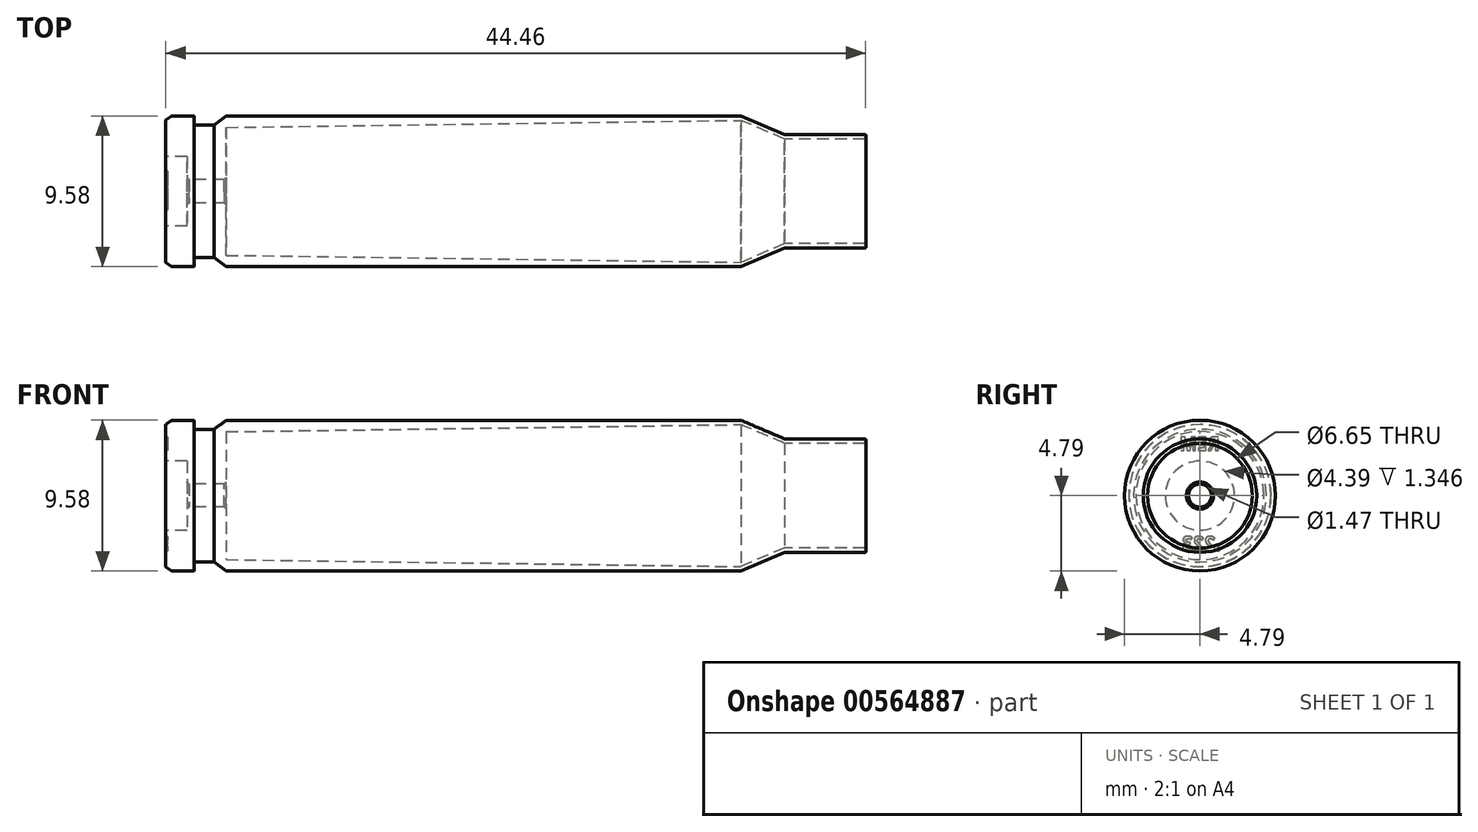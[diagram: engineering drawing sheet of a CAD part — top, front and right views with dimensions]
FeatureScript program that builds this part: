
annotation { "Feature Type Name" : "Feature", "Feature Type Description" : "" }
export const myFeature = defineFeature(function(context is Context, id is Id, definition is map)
    precondition{}
    {
        {
            var Q0;
            Q0=qCreatedBy(makeId("Front.planeOp"),FACE);
            var sketch = newSketch(context, id + "F0", { "sketchPlane" : qUnion([Q0])});
            skLineSegment(sketch, "E0", {"start": v(-35.9, 0) * mm, "end": v(-35.9, 4.52) * mm});
            skLineSegment(sketch, "E1", {"start": v(-35.9, 4.52) * mm, "end": v(-35.52, 4.79) * mm});
            skLineSegment(sketch, "E2", {"start": v(-35.52, 4.79) * mm, "end": v(-34.09, 4.79) * mm});
            skLineSegment(sketch, "E3", {"start": v(-34.09, 4.79) * mm, "end": v(-34.09, 4.22) * mm});
            skLineSegment(sketch, "E4", {"start": v(-34.09, 4.22) * mm, "end": v(-32.84, 4.22) * mm});
            skLineSegment(sketch, "E5", {"start": v(-32.84, 4.22) * mm, "end": v(-32.05, 4.79) * mm});
            skLineSegment(sketch, "E6", {"start": v(-32.05, 4.79) * mm, "end": v(0.63, 4.79) * mm});
            skLineSegment(sketch, "E7", {"start": v(0.63, 4.79) * mm, "end": v(3.4, 3.6) * mm});
            skLineSegment(sketch, "E8", {"start": v(3.4, 3.6) * mm, "end": v(8.56, 3.6) * mm});
            skLineSegment(sketch, "E9", {"start": v(8.56, 3.6) * mm, "end": v(8.56, 3.33) * mm});
            skLineSegment(sketch, "E10", {"start": v(8.56, 3.33) * mm, "end": v(3.4, 3.33) * mm});
            skLineSegment(sketch, "E11", {"start": v(3.4, 3.33) * mm, "end": v(0.63, 4.5) * mm});
            skLineSegment(sketch, "E12", {"start": v(0.63, 4.5) * mm, "end": v(-32.05, 4.06) * mm});
            skLineSegment(sketch, "E13", {"start": v(-32.05, 4.06) * mm, "end": v(-32.05, 0) * mm});
            skLineSegment(sketch, "E14", {"start": v(-32.05, 0) * mm, "end": v(-35.9, 0) * mm});
            skSolve(sketch);
        }
        {
            var Q0;
            Q0=qCreatedBy(makeId("Front.planeOp"),FACE);
            var sketch = newSketch(context, id + "F1", { "sketchPlane" : qUnion([Q0])});
            skLineSegment(sketch, "E15", {"start": v(-52.5, 0) * mm, "end": v(51.55, 0) * mm, "construction": true});
            skSolve(sketch);
        }
        {
            var Q0;
            Q0=makeQuery(id+"F0.imprint","IMPRINT",FACE,{"disambiguationData":[TD([[makeQuery(id+"F0.imprint","IMPRINT",EDGE,{"derivedFrom":sQuery(id+"F0.wireOp",EDGE,"E0")}),-1.0]])]});
            var Q1;
            Q1=sQuery(id+"F1.wireOp",EDGE,"E15");
            revolve(context, id + "F2", {"entities" : qUnion([Q0]), "axis" : qUnion([Q1]), "revolveType" : RevolveType.FULL});
        }
        {
            var Q0;
            Q0=makeQuery(id+"F2.opRevolve","SWEPT_FACE",FACE,{"disambiguationData":[OSD([sQuery(id+"F0.wireOp",EDGE,"E0")])]});
            var sketch = newSketch(context, id + "F3", { "sketchPlane" : qUnion([Q0])});
            skCircle(sketch, "E16", {"center": v(0, 0) * mm, "radius": 2.2 * mm});
            skCircle(sketch, "E17", {"center": v(0, 0) * mm, "radius": 0.73 * mm});
            skSolve(sketch);
        }
        {
            var Q0;
            Q0=makeQuery(id+"F3.imprint","IMPRINT",FACE,{"disambiguationData":[TD([[makeQuery(id+"F3.imprint","IMPRINT",EDGE,{"derivedFrom":sQuery(id+"F3.wireOp",EDGE,"E16")}),1.0]])]});
            extrude(context, id + "F4", {"entities" : qUnion([Q0]), "operationType" : NewBodyOperationType.REMOVE, "oppositeDirection" : true, "depth" : 1.35 * mm, "offsetDistance" : 25.4 * mm});
        }
        {
            var Q0;
            Q0=makeQuery(id+"F4.boolean.opBoolean","SPLIT",FACE,{"disambiguationData":[TD([makeQuery(id+"F4.opExtrude","SWEPT_FACE",FACE,{"disambiguationData":[OSD([sQuery(id+"F3.wireOp",EDGE,"E17")])]})])],"derivedFrom":makeQuery(id+"F2.opRevolve","SWEPT_FACE",FACE,{"disambiguationData":[OSD([sQuery(id+"F0.wireOp",EDGE,"E0")])]})});
            extrude(context, id + "F5", {"entities" : qUnion([Q0]), "operationType" : NewBodyOperationType.REMOVE, "oppositeDirection" : true, "depth" : 4.06 * mm, "offsetDistance" : 25.4 * mm});
        }
        {
            var Q0;
            Q0=makeQuery(id+"F4.boolean.opBoolean","COPY",EDGE,{"derivedFrom":makeQuery(id+"F4.opExtrude","CAP_EDGE",EDGE,{"disambiguationData":[OSD([sQuery(id+"F3.wireOp",EDGE,"E16")])],"isStart":true})});
            var Q1;
            Q1=makeQuery(id+"F5.boolean.opBoolean","COPY",FACE,{"derivedFrom":makeQuery(id+"F5.opExtrude","SWEPT_FACE",FACE,{"disambiguationData":[OSD([sQuery(id+"F3.wireOp",EDGE,"E17")])]})});
            chamfer(context, id + "F6", {"entities" : qUnion([Q0, Q1]), "width" : 0.13 * mm, "tangentPropagation" : true});
        }
        {
            var Q0;
            Q0=makeQuery(id+"F2.opRevolve","SWEPT_EDGE",EDGE,{"disambiguationData":[OSD([sQuery(id+"F0.wireOp",EDGE,"E6"),sQuery(id+"F0.wireOp",EDGE,"E7")])]});
            var Q1;
            Q1=makeQuery(id+"F2.opRevolve","SWEPT_EDGE",EDGE,{"disambiguationData":[OSD([sQuery(id+"F0.wireOp",EDGE,"E7"),sQuery(id+"F0.wireOp",EDGE,"E8")])]});
            fillet(context, id + "F7", {"entities" : qUnion([Q0, Q1]), "radius" : 0.05 * mm, "tangentPropagation" : true, "allowEdgeOverflow" : false});
        }
        {
            var Q0;
            Q0=makeQuery(id+"F2.opRevolve","SWEPT_EDGE",EDGE,{"disambiguationData":[OSD([sQuery(id+"F0.wireOp",EDGE,"E5"),sQuery(id+"F0.wireOp",EDGE,"E6")])]});
            var Q1;
            Q1=makeQuery(id+"F2.opRevolve","SWEPT_EDGE",EDGE,{"disambiguationData":[OSD([sQuery(id+"F0.wireOp",EDGE,"E2"),sQuery(id+"F0.wireOp",EDGE,"E3")])]});
            var Q2;
            Q2=makeQuery(id+"F2.opRevolve","SWEPT_EDGE",EDGE,{"disambiguationData":[OSD([sQuery(id+"F0.wireOp",EDGE,"E1"),sQuery(id+"F0.wireOp",EDGE,"E2")])]});
            fillet(context, id + "F8", {"entities" : qUnion([Q0, Q1, Q2]), "radius" : 0.05 * mm, "tangentPropagation" : true, "allowEdgeOverflow" : false});
        }
        {
            var Q0;
            Q0=makeQuery(id+"F4.boolean.opBoolean","SPLIT",FACE,{"disambiguationData":[TD([makeQuery(id+"F2.opRevolve","SWEPT_FACE",FACE,{"disambiguationData":[OSD([sQuery(id+"F0.wireOp",EDGE,"E1")])]})])],"derivedFrom":makeQuery(id+"F2.opRevolve","SWEPT_FACE",FACE,{"disambiguationData":[OSD([sQuery(id+"F0.wireOp",EDGE,"E0")])]})});
            var sketch = newSketch(context, id + "F9", { "sketchPlane" : qUnion([Q0])});
            skText(sketch, "E18", { "text": "REM", "fontName": "OpenSans-Bold.ttf"});
            skText(sketch, "E19", { "text": ".223", "fontName": "OpenSans-Bold.ttf"});
            const initialGuessF9  = {"E18": [-0.00128, 0.00287, 1, 0, 0.00086], "E19": [-0.00135, -0.00349, 1, 0, 0.0009]};
            skSetInitialGuess(sketch, initialGuessF9);
            skSolve(sketch);
        }
        {
            var Q0;
            Q0=qSketchRegion(id+"F9",true);
            extrude(context, id + "F10", {"entities" : qUnion([Q0]), "operationType" : NewBodyOperationType.REMOVE, "oppositeDirection" : true, "depth" : 0.13 * mm, "offsetDistance" : 25.4 * mm});
        }
        {
            var Q0;
            Q0=makeQuery(id+"F2.opRevolve","SWEPT_EDGE",EDGE,{"disambiguationData":[OSD([sQuery(id+"F0.wireOp",EDGE,"E8"),sQuery(id+"F0.wireOp",EDGE,"E9")])]});
            var Q1;
            Q1=makeQuery(id+"F2.opRevolve","SWEPT_EDGE",EDGE,{"disambiguationData":[OSD([sQuery(id+"F0.wireOp",EDGE,"E9"),sQuery(id+"F0.wireOp",EDGE,"E10")])]});
            fillet(context, id + "F11", {"entities" : qUnion([Q0, Q1]), "radius" : 0.05 * mm, "tangentPropagation" : true, "allowEdgeOverflow" : false});
        }
    });
